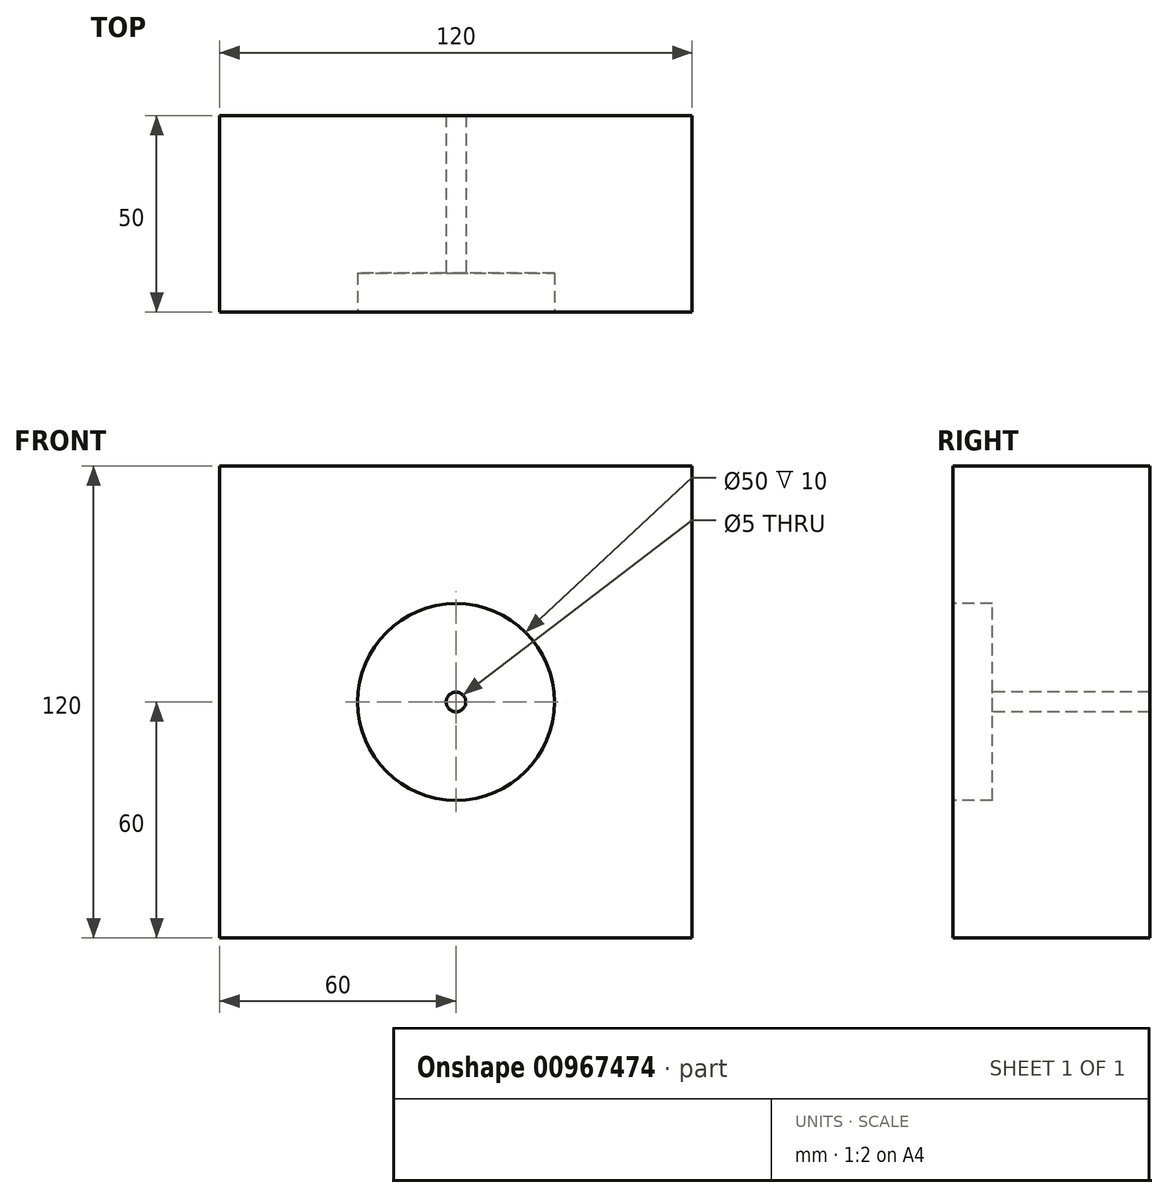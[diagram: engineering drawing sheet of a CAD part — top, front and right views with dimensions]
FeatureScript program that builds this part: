
annotation { "Feature Type Name" : "Feature", "Feature Type Description" : "" }
export const myFeature = defineFeature(function(context is Context, id is Id, definition is map)
    precondition{}
    {
        {
            var Q0;
            Q0=qCreatedBy(makeId("Front.planeOp"),FACE);
            var sketch = newSketch(context, id + "F0", { "sketchPlane" : qUnion([Q0])});
            skLineSegment(sketch, "E0.bottom", {"start": v(60, 60) * mm, "end": v(-60, 60) * mm});
            skLineSegment(sketch, "E0.top", {"start": v(60, -60) * mm, "end": v(-60, -60) * mm});
            skLineSegment(sketch, "E0.left", {"start": v(60, 60) * mm, "end": v(60, -60) * mm});
            skLineSegment(sketch, "E0.right", {"start": v(-60, 60) * mm, "end": v(-60, -60) * mm});
            skPoint(sketch, "E0.middle", {"position": v(0, 0) * mm});
            skSolve(sketch);
        }
        {
            var Q0;
            Q0=makeQuery(id+"F0.imprint","IMPRINT",FACE,{"disambiguationData":[TD([[makeQuery(id+"F0.imprint","IMPRINT",EDGE,{"derivedFrom":sQuery(id+"F0.wireOp",EDGE,"E0.bottom")}),1.0]])]});
            extrude(context, id + "F1", {"entities" : qUnion([Q0]), "endBound" : BoundingType.SYMMETRIC, "depth" : 50 * mm, "offsetDistance" : 25 * mm});
        }
        {
            var Q0;
            Q0=makeQuery(id+"F1.opExtrude","CAP_FACE",FACE,{"disambiguationData":[OSD([sQuery(id+"F0.wireOp",EDGE,"E0.bottom"),sQuery(id+"F0.wireOp",EDGE,"E0.top"),sQuery(id+"F0.wireOp",EDGE,"E0.left"),sQuery(id+"F0.wireOp",EDGE,"E0.right")])],"isStart":false});
            var sketch = newSketch(context, id + "F2", { "sketchPlane" : qUnion([Q0])});
            skCircle(sketch, "E1", {"center": v(0, 0) * mm, "radius": 25 * mm});
            skSolve(sketch);
        }
        {
            var Q0;
            Q0 = qSketchRegion(id + "F2", true);
            extrude(context, id + "F3", {"entities" : qUnion([Q0]), "operationType" : NewBodyOperationType.REMOVE, "oppositeDirection" : true, "depth" : 10 * mm, "offsetDistance" : 25 * mm});
        }
        {
            var Q0;
            Q0=makeQuery(id+"F3.boolean.opBoolean","COPY",FACE,{"derivedFrom":makeQuery(id+"F3.opExtrude","CAP_FACE",FACE,{"disambiguationData":[OSD([sQuery(id+"F2.wireOp",EDGE,"E1")])],"isStart":false})});
            var sketch = newSketch(context, id + "F4", { "sketchPlane" : qUnion([Q0])});
            skPoint(sketch, "E2", {"position": v(0, 0) * mm});
            skSolve(sketch);
        }
        {
            var Q0;
            Q0=sQuery(id+"F4.wireOp",VERTEX,"E2");
            var Q1;
            Q1=makeQuery(id+"F1.opExtrude","SWEPT_BODY",BODY,{"disambiguationData":[OSD([sQuery(id+"F0.wireOp",EDGE,"E0.bottom"),sQuery(id+"F0.wireOp",EDGE,"E0.top"),sQuery(id+"F0.wireOp",EDGE,"E0.left"),sQuery(id+"F0.wireOp",EDGE,"E0.right")])]});
            hole(context, id + "F5", {"style" : HoleStyle.SIMPLE, "endStyle" : HoleEndStyle.THROUGH, "standardTappedOrClearance" : lookupTablePath({ "standard" : "ISO", "engagement" : "75%", "pitch" : "1 mm", "size" : "M6", "type" : "Tapped" }), "standardBlindInLast" : lookupTablePath({ "standard" : "ISO", "fit" : "Normal", "engagement" : "75%", "pitch" : "1 mm", "size" : "M6", "type" : "Clearance & tapped" }), "holeDiameter" : 5 * mm, "majorDiameter" : 6 * mm, "showTappedDepth" : true, "isTappedThrough" : true, "tappedDepth" : 12 * mm, "tapClearance" : 3, "locations" : qUnion([Q0]), "scope" : qUnion([Q1])});
        }
    });
